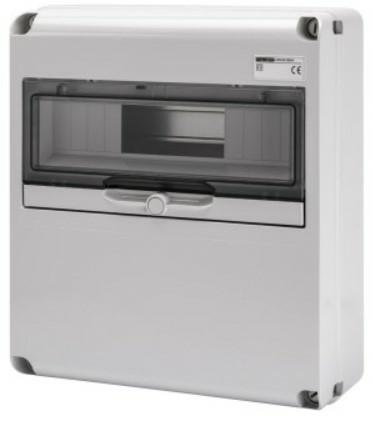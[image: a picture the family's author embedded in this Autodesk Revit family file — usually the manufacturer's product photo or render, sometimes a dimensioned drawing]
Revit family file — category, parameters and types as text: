
# Revit family: Building-QuadriIEC309-GEWISS-68QDIN-QUADRI-14MOD_CIECO
name_source: partatom
category: Apparecchi elettrici
units: mm (PartAtom-declared; Revit-internal decimal feet)

## family parameters
Condiviso = No
Host = Superficie
Mantenere orientamento annotazione = Sì
Punto di calcolo locali = Sì
Quota connettore circolare = Usa diametro
Taglio con vuoti quando caricato = No
Tipo di parte = Normale

## types (1)
- GW68004N - Q-DIN 14M COP.CIECO 360x320x135 IP65
    Catalogo = BUILDING
    Catalogo Serie = 68 QDIN
    Classe isolamento = II
    Codice EAN = 8011564744752
    Codice Electrocod = 2242
    Colore = Grigio RAL 7035
    Conformità normativa = EN 60208 - EN 60670-1 - IEC 60670-24
    Descrizione = Q-DIN 14M COP.CIECO 360x320x135 IP65
    Glow Wire Test = 650°C
    Grado di protezione = IP65
    IDF = 9309c37a-fa6c-48e9-828f-dc0c7c013670
    IDT = d585780b-ac8c-4f69-a7b1-54dd751465a2
    Immagine tipo = GW68004N.jpg
    L_Moduli = 266 mm  [stored 0.872703 ft]
    Modello = GW68004N
    N. coperchi ciechi in dotazione = -
    N. mod. EN 50022 = 14
    N. prese alloggiabili = Coperchio cieco
    N_Moduli = 14 mm  [stored 0.0459318 ft]
    POMELLO = bianco
    PRESA = rosso
    Potenza dissipabile A (W) = 24
    Potenza dissipabile B (W) = 64
    Produttore = GEWISS S.p.A.
    Prospetto di default = 1219 mm
    Resistenza agli urti = IK09
    SEO = Quadretto
    STRUTTURA = RAL - 7035
    STRUTTURA ALTA = Poche
    Scheda Tecnica = https://www.gewiss.com
    Spostamento_S = 1000 mm  [stored 3.28084 ft]
    Temperatura di utilizzo = -25 +40 °C
    Termopressione con biglia = 70 °C
    Tipo versione = Vuoto
    Tipologia di installazione = Da parete
    URL = https://www.gewiss.com
    VETRO = Vetro
    Versione file RFA = 21.5

note: [stored X ft] marks values corroborated as IEEE doubles in the binary element streams (Revit-internal decimal feet)

## geometry (parser evidence)
native form markers: Sweep x2
no freeform markers — native parametric forms only
